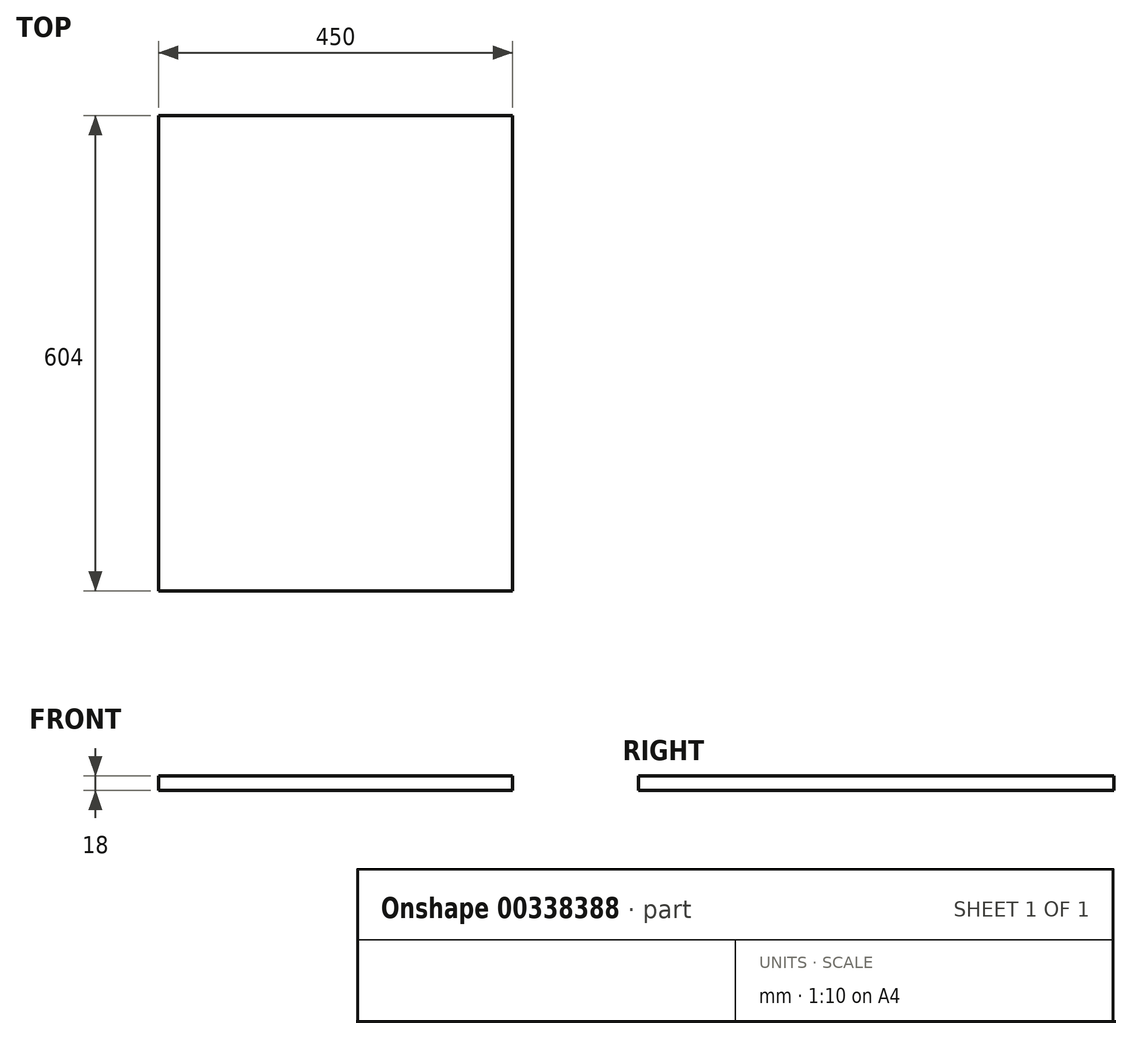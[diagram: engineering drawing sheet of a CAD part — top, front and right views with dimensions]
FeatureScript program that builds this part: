
annotation { "Feature Type Name" : "Feature", "Feature Type Description" : "" }
export const myFeature = defineFeature(function(context is Context, id is Id, definition is map)
    precondition{}
    {
        {
            var Q0;
            Q0=qCreatedBy(makeId("Top.planeOp"),FACE);
            var sketch = newSketch(context, id + "F0", { "sketchPlane" : qUnion([Q0])});
            skLineSegment(sketch, "E0.bottom", {"start": v(-225, -302) * mm, "end": v(225, -302) * mm});
            skLineSegment(sketch, "E0.top", {"start": v(-225, 302) * mm, "end": v(225, 302) * mm});
            skLineSegment(sketch, "E0.left", {"start": v(-225, -302) * mm, "end": v(-225, 302) * mm});
            skLineSegment(sketch, "E0.right", {"start": v(225, -302) * mm, "end": v(225, 302) * mm});
            skPoint(sketch, "E0.middle", {"position": v(0, 0) * mm});
            skSolve(sketch);
        }
        {
            var Q0;
            Q0=makeQuery(id+"F0.imprint","IMPRINT",FACE,{"disambiguationData":[TD([[makeQuery(id+"F0.imprint","IMPRINT",EDGE,{"derivedFrom":sQuery(id+"F0.wireOp",EDGE,"E0.bottom")}),1.0]])]});
            extrude(context, id + "F1", {"entities" : qUnion([Q0]), "depth" : 18 * mm});
        }
    });
